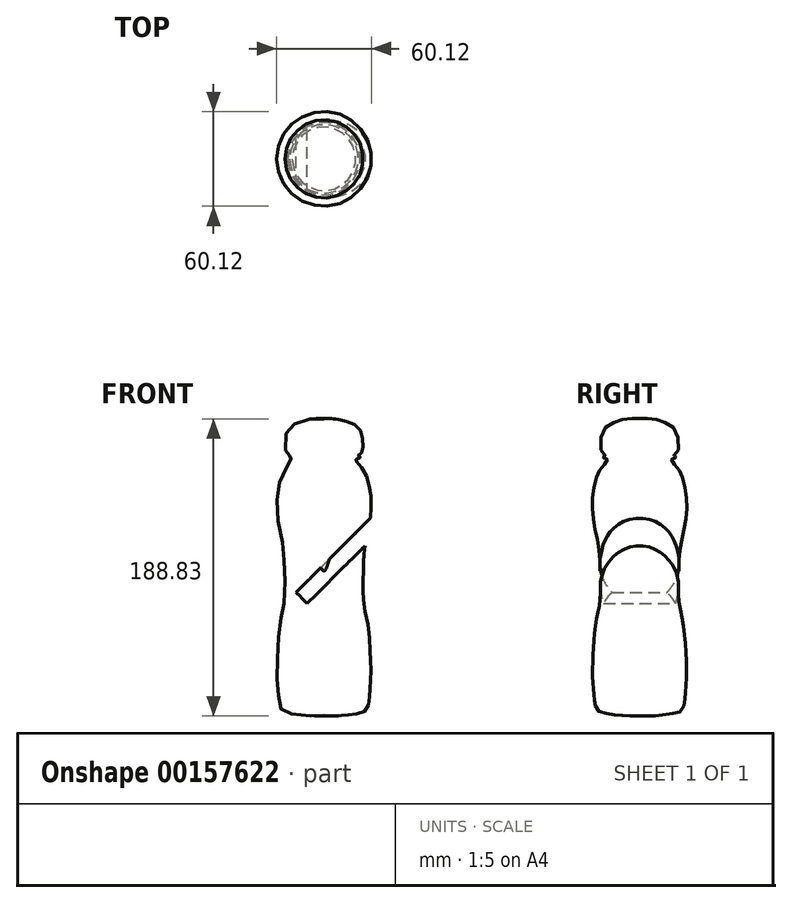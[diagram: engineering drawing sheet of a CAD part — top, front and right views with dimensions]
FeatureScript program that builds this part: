
annotation { "Feature Type Name" : "Feature", "Feature Type Description" : "" }
export const myFeature = defineFeature(function(context is Context, id is Id, definition is map)
    precondition{}
    {
        {
            var Q0;
            Q0=qCreatedBy(makeId("Front.planeOp"),FACE);
            var sketch = newSketch(context, id + "F0", { "sketchPlane" : qUnion([Q0])});
            skLineSegment(sketch, "E0", {"start": v(0, -88.7) * mm, "end": v(0, 99.42) * mm});
            skFitSpline(sketch, "E1", {"points": [v(0, 99.42) * mm, v(-8.8, 99.42) * mm, v(-19.41, 95.88) * mm, v(-23.92, 90.25) * mm, v(-24.24, 78.66) * mm, v(-22.63, 77.05) * mm, v(-21.83, 76.4) * mm, v(-22.95, 75.28) * mm, v(-22.15, 74.48) * mm, v(-20.22, 73.67) * mm, v(-24.56, 67.88) * mm, v(-28.9, 56.3) * mm, v(-29.82, 39.63) * mm, v(-26.07, 18.83) * mm, v(-25.05, 4.68) * mm, v(-25.22, -17.49) * mm, v(-27.26, -27.55) * mm, v(-29.24, -45.48) * mm, v(-29.75, -64.57) * mm, v(-28.9, -76.85) * mm, v(-27.2, -85.03) * mm, v(-22.93, -87.25) * mm, v(-7.25, -89.13) * mm, v(0, -88.7) * mm], "startDerivative": vector(-195.12, 15.93) * mm, "endDerivative": vector(157.6, 19.68) * mm});
            skSolve(sketch);
        }
        {
            var Q0;
            Q0=makeQuery(id+"F0.imprint","IMPRINT",FACE,{"disambiguationData":[TD([[makeQuery(id+"F0.imprint","IMPRINT",EDGE,{"derivedFrom":sQuery(id+"F0.wireOp",EDGE,"E0")}),1.0]])]});
            var Q1;
            Q1=sQuery(id+"F0.wireOp",EDGE,"E0");
            revolve(context, id + "F1", {"entities" : qUnion([Q0]), "axis" : qUnion([Q1]), "revolveType" : RevolveType.FULL});
        }
        {
            var Q0;
            Q0=qCreatedBy(makeId("Right.planeOp"),FACE);
            var sketch = newSketch(context, id + "F2", { "sketchPlane" : qUnion([Q0])});
            skLineSegment(sketch, "E2", {"start": v(-74.45, 0) * mm, "end": v(74.45, 0) * mm, "construction": true});
            skSolve(sketch);
        }
        {
            var Q0;
            Q0=sQuery(id+"F2.wireOp",EDGE,"E2");
            cPlane(context, id + "F3", {"entities" : qUnion([Q0]), "cplaneType" : CPlaneType.LINE_ANGLE, "offset" : 25 * mm, "angle" : 45 * degree, "width" : 150 * mm, "height" : 150 * mm});
        }
        {
            var Q0;
            Q0=qCreatedBy(id+"F3.planeOp",FACE);
            var sketch = newSketch(context, id + "F4", { "sketchPlane" : qUnion([Q0])});
            skLineSegment(sketch, "E3.bottom", {"start": v(-25, -5) * mm, "end": v(25, -5) * mm});
            skLineSegment(sketch, "E3.top", {"start": v(-25, 5) * mm, "end": v(25, 5) * mm});
            skLineSegment(sketch, "E3.left", {"start": v(-25, -5) * mm, "end": v(-25, 5) * mm});
            skLineSegment(sketch, "E3.right", {"start": v(25, -5) * mm, "end": v(25, 5) * mm});
            skPoint(sketch, "E3.middle", {"position": v(0, 0) * mm});
            skSolve(sketch);
        }
        {
            var Q0;
            Q0=makeQuery(id+"F4.imprint","IMPRINT",FACE,{"disambiguationData":[TD([[makeQuery(id+"F4.imprint","IMPRINT",EDGE,{"derivedFrom":sQuery(id+"F4.wireOp",EDGE,"E3.bottom")}),1.0]])]});
            extrude(context, id + "F5", {"entities" : qUnion([Q0]), "operationType" : NewBodyOperationType.REMOVE, "oppositeDirection" : true, "depth" : 20 * mm, "hasSecondDirection" : true, "secondDirectionOppositeDirection" : false, "secondDirectionDepth" : 80 * mm});
        }
    });
